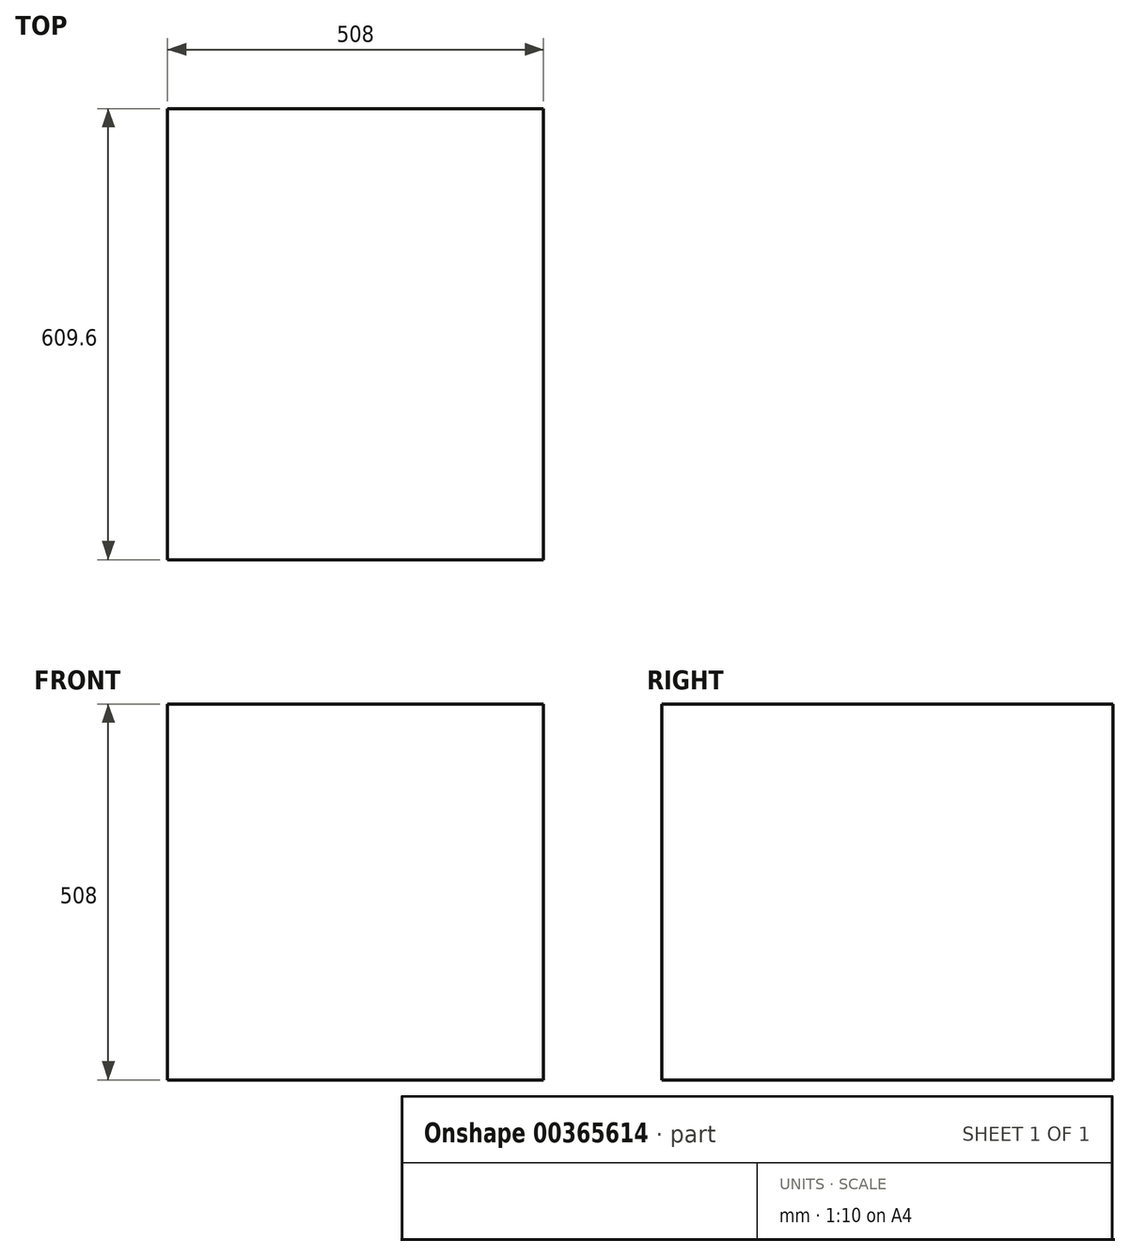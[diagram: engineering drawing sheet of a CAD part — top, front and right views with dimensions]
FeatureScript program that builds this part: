
annotation { "Feature Type Name" : "Feature", "Feature Type Description" : "" }
export const myFeature = defineFeature(function(context is Context, id is Id, definition is map)
    precondition{}
    {
        {
            var Q0;
            Q0=qCreatedBy(makeId("Front.planeOp"),FACE);
            var sketch = newSketch(context, id + "F0", { "sketchPlane" : qUnion([Q0])});
            skLineSegment(sketch, "E0.bottom", {"start": v(254, -254) * mm, "end": v(-254, -254) * mm});
            skLineSegment(sketch, "E0.top", {"start": v(254, 254) * mm, "end": v(-254, 254) * mm});
            skLineSegment(sketch, "E0.left", {"start": v(254, -254) * mm, "end": v(254, 254) * mm});
            skLineSegment(sketch, "E0.right", {"start": v(-254, -254) * mm, "end": v(-254, 254) * mm});
            skPoint(sketch, "E0.middle", {"position": v(0, 0) * mm});
            skSolve(sketch);
        }
        {
            var Q0;
            Q0 = qSketchRegion(id + "F0", true);
            extrude(context, id + "F1", {"entities" : qUnion([Q0]), "depth" : 609.6 * mm, "offsetDistance" : 25.4 * mm});
        }
    });
